# Revit family: M125-E069xxx-DB
name_source: partatom
category: Leuchten
units: mm (PartAtom-declared; Revit-internal decimal feet)

## family parameters
Basisbauteil = Fläche
Beim Laden mit Abzugskörper schneiden = Nein
Bemaßung runder Anschluss = Durchmesser verwenden
Gemeinsam genutzt = Nein
Lichtquelle = Ja
OmniClass-Nummer = 23.80.70.11
OmniClass-Titel = Luminaries for Internal Lighting
Raumberechnungspunkt = Nein
Teiletyp = Normal

## types (2) — shared parameters
Baugruppenkennzeichen = D5020200
Emissionsform beim Rendern sichtbar = Nein
Farbfilter = 16777215
Farbtemperaturverschiebung bei Dämpfen der Lampe = <Keine Auswahl>
Hersteller = RIDI Leuchten GmbH
Lampe = LED
Neigungswinkel = 90.00°
Scheinlast = 18 VA
URL = www.ridi.de
Von Breite des Rechtecks ausssenden = 616 mm  [stored 2.021 ft]
Von Länge des Rechtecks aussenden = 95 mm
brand = RIDI
conformity mark = CE
electrical safety class = 1
height = 99 mm  [stored 0.324803 ft]
ingress protection (IP) code = IP65
length = 720 mm  [stored 2.3622 ft]
nominal frequency = 50-60Hz
nominal voltage = 230
rated input power = 18
voltage type (AC, DC, UC) = AC
weight = 5.9 kg
width = 149 mm  [stored 0.488845 ft]
zero-valued in all types: Vorgabe-Ansicht

## per-type parameters (varying)
| type | Datei für fotometrisches Netz | Modell |
| M125-E069 NDWS840MPO0225-DB | M125_MPO.IES | 6068073 |
| M125-E069 NDWS840S0200-DB | M125-S.IES | 6068039 |

note: column(s) folded — value = type name in every type: product name

note: [stored X ft] marks values corroborated as IEEE doubles in the binary element streams (Revit-internal decimal feet)
